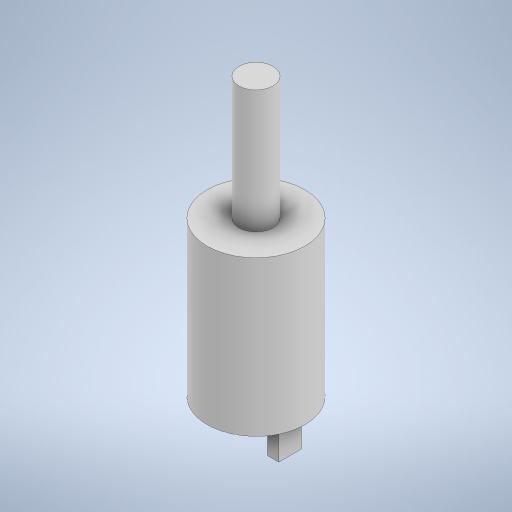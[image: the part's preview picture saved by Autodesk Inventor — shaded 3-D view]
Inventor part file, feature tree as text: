
AUTODESK INVENTOR PART (.ipt)
format: ipt  version: 2023 (Build 270158030, 158C)  size: 250,880 bytes
history: native  units: in
note: dims shown in document units (in); Inventor stores cm internally (conversion verified against a paired STEP export)
features: extrude x3, sketch x3
ambient origin geometry x8: Origin, YZ Plane, XZ Plane, XY Plane, X Axis, Y Axis, Z Axis, Center Point
bodies: Solid1 (feature_tree)
feature tree (6):
  extrude  "Extrusion1"  Depth=2.6772in TaperAngle=0.0deg
  extrude  "Extrusion2"  Depth=2.126in TaperAngle=0.0deg
  extrude  "Extrusion3"  Depth=0.1969in
  sketch  "Sketch1"  dims[d0=1.6929in d1=2.6772in d2=0.0in]
  sketch  "Sketch2"  dims[d3=0.5906in d4=2.126in d5=0.0in]
  sketch  "Sketch3"  dims[d6=0.3937in d7=0.1969in d8=0.7874in d9=0.5906in d10=0.0in]
